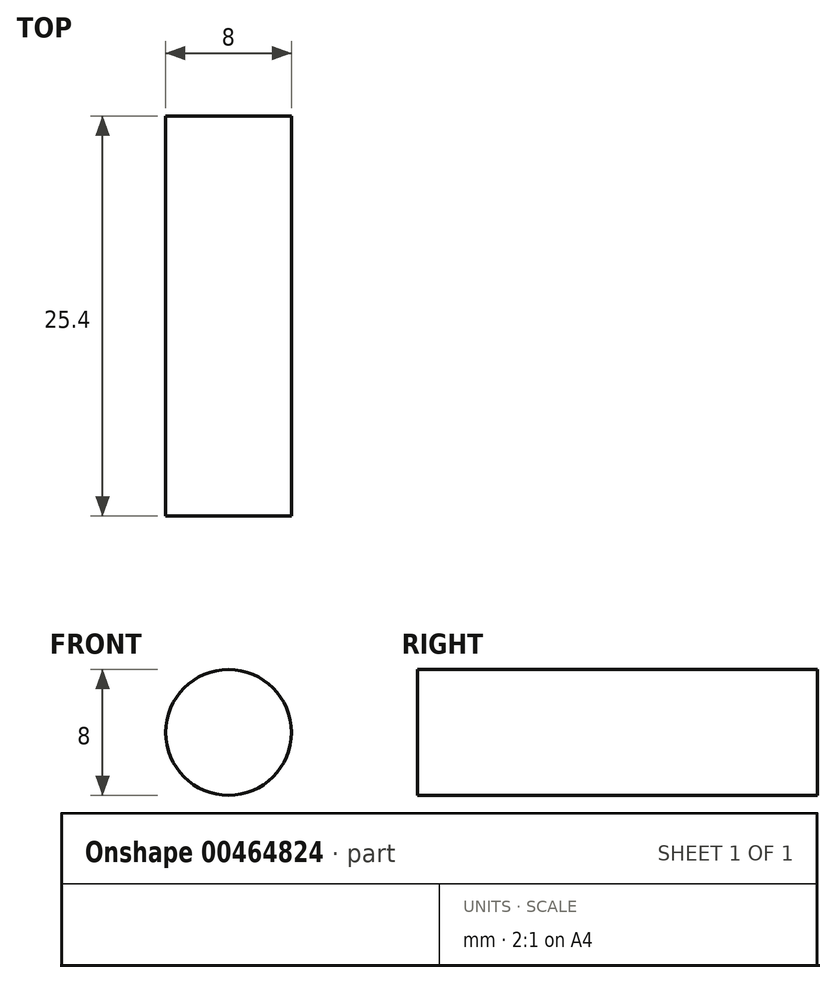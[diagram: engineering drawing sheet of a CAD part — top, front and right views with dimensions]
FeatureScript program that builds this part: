
annotation { "Feature Type Name" : "Feature", "Feature Type Description" : "" }
export const myFeature = defineFeature(function(context is Context, id is Id, definition is map)
    precondition{}
    {
        {
            var Q0;
            Q0=qCreatedBy(makeId("Front.planeOp"),FACE);
            var sketch = newSketch(context, id + "F0", { "sketchPlane" : qUnion([Q0])});
            skCircle(sketch, "E0", {"center": v(0, 0) * mm, "radius": 4 * mm});
            skSolve(sketch);
        }
        {
            var Q0;
            Q0 = qSketchRegion(id + "F0", true);
            extrude(context, id + "F1", {"entities" : qUnion([Q0]), "depth" : 25.4 * mm});
        }
    });
